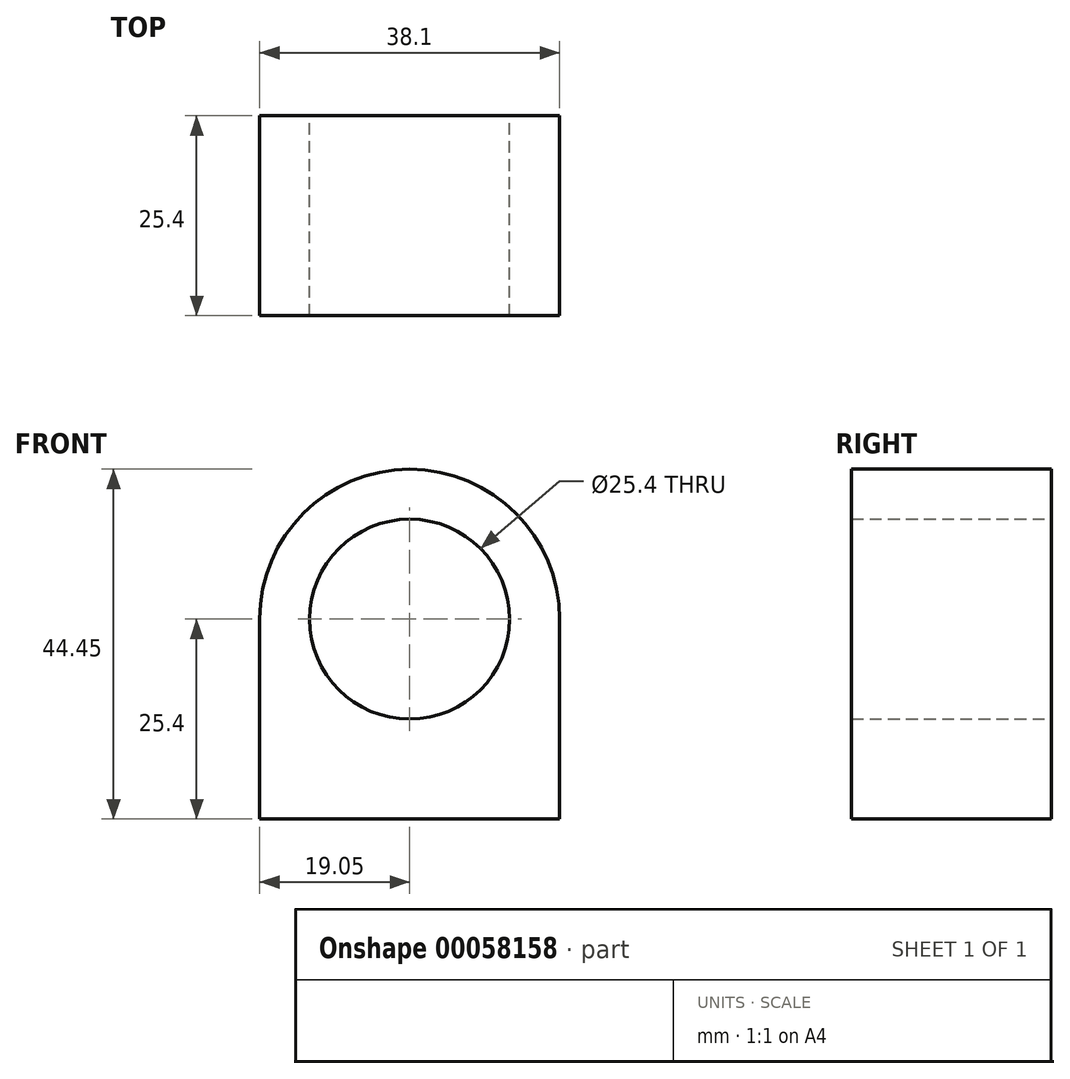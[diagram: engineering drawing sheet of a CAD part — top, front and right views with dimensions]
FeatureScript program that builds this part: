
annotation { "Feature Type Name" : "Feature", "Feature Type Description" : "" }
export const myFeature = defineFeature(function(context is Context, id is Id, definition is map)
    precondition{}
    {
        {
            var Q0;
            Q0=qCreatedBy(makeId("Front.planeOp"),FACE);
            var sketch = newSketch(context, id + "F0", { "sketchPlane" : qUnion([Q0])});
            skCircle(sketch, "E0", {"center": v(0, 0) * mm, "radius": 12.7 * mm});
            skArc(sketch, "E1", {"start": v(19.05, 0) * mm, "mid": v(0, 19.05) * mm, "end": v(-19.05, 0) * mm});
            skLineSegment(sketch, "E2", {"start": v(-19.05, 0) * mm, "end": v(-19.05, -25.4) * mm});
            skLineSegment(sketch, "E3", {"start": v(-19.05, -25.4) * mm, "end": v(19.05, -25.4) * mm});
            skLineSegment(sketch, "E4", {"start": v(19.05, -25.4) * mm, "end": v(19.05, 0) * mm});
            skSolve(sketch);
        }
        {
            var Q0;
            Q0=makeQuery(id+"F0.imprint","IMPRINT",FACE,{"disambiguationData":[TD([[makeQuery(id+"F0.imprint","IMPRINT",EDGE,{"derivedFrom":sQuery(id+"F0.wireOp",EDGE,"E0")}),-1.0]])]});
            extrude(context, id + "F1", {"entities" : qUnion([Q0]), "depth" : 25.4 * mm});
        }
    });
